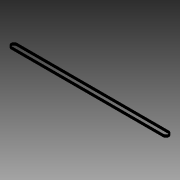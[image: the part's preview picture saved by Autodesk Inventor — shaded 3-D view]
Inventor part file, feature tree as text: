
AUTODESK INVENTOR PART (.ipt)
format: ipt  version: 2013 (Build 170138000, 138)  size: 88,576 bytes
history: native  units: mm
features: extrude x1, sketch x1
ambient origin geometry x8: Origin, YZ Plane, XZ Plane, XY Plane, X Axis, Y Axis, Z Axis, Center Point
bodies: Solid1 (feature_tree)
feature tree (2):
  extrude  "Extrusion1"  Depth=12.0mm
  sketch  "Sketch1"  dims[d0=12.0mm d2=12.0mm d3=359.0mm d4=1.2mm d5=6.0mm d6=0.0mm]
